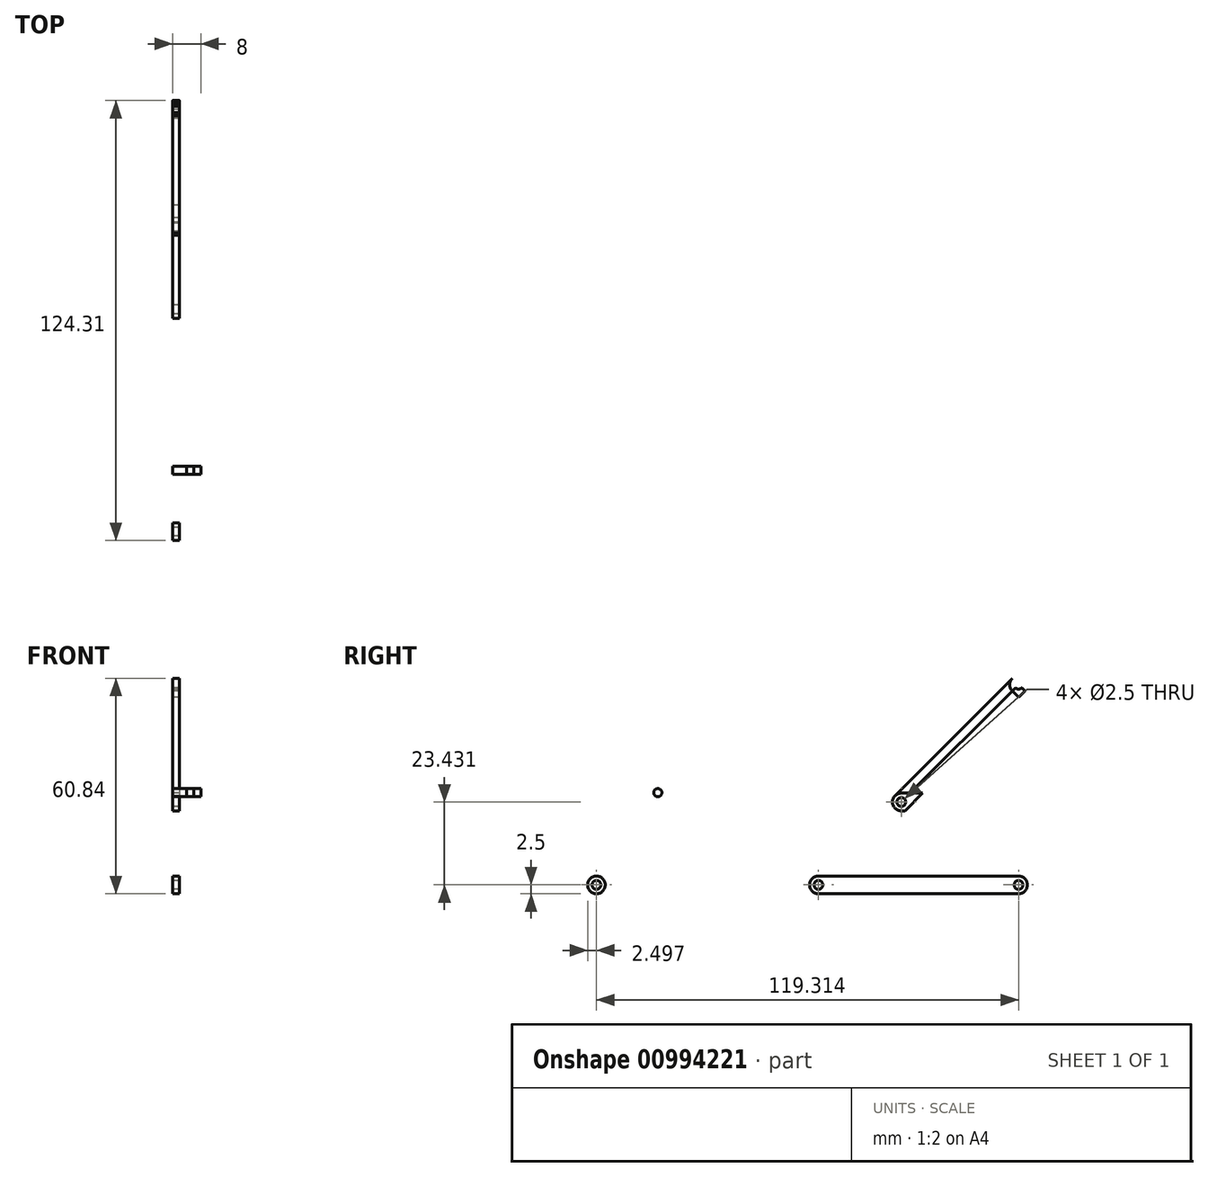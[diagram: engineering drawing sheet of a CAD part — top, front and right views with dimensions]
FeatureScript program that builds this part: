
annotation { "Feature Type Name" : "Feature", "Feature Type Description" : "" }
export const myFeature = defineFeature(function(context is Context, id is Id, definition is map)
    precondition{}
    {
        {
            assignVariable(context, id + "F0", {"name" : "thick", "anyValue" : 2});
        }
        {
            assignVariable(context, id + "F1", {"name" : "w", "anyValue" : 5});
        }
        {
            var Q0;
            Q0=qCreatedBy(makeId("Right.planeOp"),FACE);
            var sketch = newSketch(context, id + "F2", { "sketchPlane" : qUnion([Q0])});
            skLineSegment(sketch, "E0", {"start": v(0, 0) * mm, "end": v(-56.57, 56.57) * mm});
            skArc(sketch, "E1.0.startCap", {"start": v(1.77, 1.77) * mm, "mid": v(1.77, -1.77) * mm, "end": v(-1.77, -1.77) * mm});
            skArc(sketch, "E1.0.endCap", {"start": v(-58.34, 54.8) * mm, "mid": v(-58.34, 58.34) * mm, "end": v(-54.8, 58.34) * mm});
            skLineSegment(sketch, "E1.0.left", {"start": v(-1.77, -1.77) * mm, "end": v(-58.34, 54.8) * mm});
            skLineSegment(sketch, "E1.0.right", {"start": v(1.77, 1.77) * mm, "end": v(-54.8, 58.34) * mm});
            skLineSegment(sketch, "E2", {"start": v(-56.57, 56.57) * mm, "end": v(-113.14, 0) * mm});
            skArc(sketch, "E3.0.startCap", {"start": v(-58.34, 58.34) * mm, "mid": v(-54.8, 58.34) * mm, "end": v(-54.8, 54.8) * mm});
            skArc(sketch, "E3.0.endCap", {"start": v(-111.37, -1.77) * mm, "mid": v(-114.9, -1.77) * mm, "end": v(-114.9, 1.77) * mm});
            skLineSegment(sketch, "E3.0.left", {"start": v(-54.8, 54.8) * mm, "end": v(-111.37, -1.77) * mm});
            skLineSegment(sketch, "E3.0.right", {"start": v(-58.34, 58.34) * mm, "end": v(-114.9, 1.77) * mm});
            skLineSegment(sketch, "E4", {"start": v(0, 0) * mm, "end": v(230.96, 0) * mm, "construction": true});
            skLineSegment(sketch, "E5", {"start": v(-56.57, 0) * mm, "end": v(-113.14, 0) * mm});
            skArc(sketch, "E6.0.startCap", {"start": v(-56.57, 2.5) * mm, "mid": v(-54.07, 0) * mm, "end": v(-56.57, -2.5) * mm});
            skArc(sketch, "E6.0.endCap", {"start": v(-113.14, -2.5) * mm, "mid": v(-115.64, 0) * mm, "end": v(-113.14, 2.5) * mm});
            skLineSegment(sketch, "E6.0.left", {"start": v(-56.57, -2.5) * mm, "end": v(-113.14, -2.5) * mm});
            skLineSegment(sketch, "E6.0.right", {"start": v(-56.57, 2.5) * mm, "end": v(-113.14, 2.5) * mm});
            skLineSegment(sketch, "E7", {"start": v(-56.57, 56.57) * mm, "end": v(-56.57, -230.62) * mm, "construction": true});
            skLineSegment(sketch, "E8", {"start": v(0, 0) * mm, "end": v(0, 80) * mm, "construction": true});
            skArc(sketch, "E9", {"start": v(0, 0) * mm, "mid": v(-36.42, 8.77) * mm, "end": v(-64.86, 33.16) * mm, "construction": true});
            skLineSegment(sketch, "E10", {"start": v(-56.57, 23.43) * mm, "end": v(-89.7, 23.43) * mm});
            skArc(sketch, "E11.0.startCap", {"start": v(-56.57, 25.93) * mm, "mid": v(-54.07, 23.43) * mm, "end": v(-56.57, 20.93) * mm});
            skArc(sketch, "E11.0.endCap", {"start": v(-89.7, 20.93) * mm, "mid": v(-92.2, 23.43) * mm, "end": v(-89.7, 25.93) * mm});
            skLineSegment(sketch, "E11.0.left", {"start": v(-56.57, 20.93) * mm, "end": v(-89.7, 20.93) * mm});
            skLineSegment(sketch, "E11.0.right", {"start": v(-56.57, 25.93) * mm, "end": v(-89.7, 25.93) * mm});
            skLineSegment(sketch, "E12", {"start": v(-56.57, 23.43) * mm, "end": v(-23.43, 23.43) * mm, "construction": true});
            skCircle(sketch, "E13", {"center": v(-175.88, 0) * mm, "radius": 2.5 * mm});
            skCircle(sketch, "E14", {"center": v(-158.53, 26.07) * mm, "radius": 1.15 * mm});
            skSolve(sketch);
        }
        {
            var Q0;
            Q0=makeQuery(id+"F2.imprint","IMPRINT",FACE,{"disambiguationData":[TD([[makeQuery(id+"F2.imprint","IMPRINT",EDGE,{"derivedFrom":sQuery(id+"F2.wireOp",EDGE,"E1.0.startCap")}),-1.0]])]});
            var Q1;
            {var subQ0=sQuery(id+"F2.wireOp",EDGE,"E2");var subQ1=sQuery(id+"F2.wireOp",EDGE,"E0");var subQ2=makeQuery(id+"F2.imprint","INTERSECT",VERTEX,{"derivedFrom":[subQ1,subQ0]});Q1=makeQuery(id+"F2.imprint","IMPRINT",FACE,{"disambiguationData":[TD([[makeQuery(id+"F2.imprint","IMPRINT",EDGE,{"disambiguationData":[TD([[subQ2,1.0]])],"derivedFrom":subQ1}),1.0]])]});}
            var Q2;
            {var subQ3=sQuery(id+"F2.wireOp",EDGE,"E1.0.endCap");Q2=makeQuery(id+"F2.imprint","IMPRINT",FACE,{"disambiguationData":[TD([[makeQuery(id+"F2.imprint","IMPRINT",EDGE,{"derivedFrom":subQ3}),-1.0]])]});}
            extrude(context, id + "F3", {"entities" : qUnion([Q0, Q1, Q2]), "depth" : (getVariable(context, 'thick')) * mm, "offsetDistance" : 25 * mm});
        }
        {
            var Q0;
            {var subQ2=sQuery(id+"F2.wireOp",EDGE,"E3.0.endCap");Q0=makeQuery(id+"F2.imprint","IMPRINT",FACE,{"disambiguationData":[TD([[makeQuery(id+"F2.imprint","IMPRINT",EDGE,{"derivedFrom":subQ2}),1.0]])]});}
            var Q1;
            {var subQ0=sQuery(id+"F2.wireOp",EDGE,"E5");var subQ1=sQuery(id+"F2.wireOp",EDGE,"E2");var subQ2=makeQuery(id+"F2.imprint","INTERSECT",VERTEX,{"derivedFrom":[subQ1,subQ0]});Q1=makeQuery(id+"F2.imprint","IMPRINT",FACE,{"disambiguationData":[TD([[makeQuery(id+"F2.imprint","IMPRINT",EDGE,{"disambiguationData":[TD([[subQ2,1.0]])],"derivedFrom":subQ1}),1.0]])]});}
            var Q2;
            {var subQ5=sQuery(id+"F2.wireOp",EDGE,"E3.0.endCap");Q2=makeQuery(id+"F2.imprint","IMPRINT",FACE,{"disambiguationData":[TD([[makeQuery(id+"F2.imprint","IMPRINT",EDGE,{"derivedFrom":subQ5}),-1.0]])]});}
            extrude(context, id + "F4", {"entities" : qUnion([Q0, Q1, Q2]), "depth" : (getVariable(context, 'thick')) * mm, "offsetDistance" : 25 * mm});
        }
        {
            var Q0;
            Q0=sQuery(id+"F2.wireOp",VERTEX,"E5.start");
            var Q1;
            Q1=sQuery(id+"F2.wireOp",VERTEX,"E2.end");
            var Q2;
            Q2=sQuery(id+"F2.wireOp",VERTEX,"E0.start");
            var Q3;
            Q3=sQuery(id+"F2.wireOp",VERTEX,"E0.end");
            var Q4;
            Q4=makeQuery(id+"F3.opExtrude","SWEPT_BODY",BODY,{"disambiguationData":[OSD([sQuery(id+"F2.wireOp",EDGE,"E1.0.startCap"),sQuery(id+"F2.wireOp",EDGE,"E1.0.endCap"),sQuery(id+"F2.wireOp",EDGE,"E1.0.left"),sQuery(id+"F2.wireOp",EDGE,"E1.0.right"),sQuery(id+"F2.wireOp",EDGE,"E3.0.startCap")])]});
            var Q5;
            Q5=makeQuery(id+"F4.opExtrude","SWEPT_BODY",BODY,{"disambiguationData":[OSD([sQuery(id+"F2.wireOp",EDGE,"E6.0.startCap"),sQuery(id+"F2.wireOp",EDGE,"E6.0.endCap"),sQuery(id+"F2.wireOp",EDGE,"E6.0.left"),sQuery(id+"F2.wireOp",EDGE,"E6.0.right")])]});
            hole(context, id + "F5", {"style" : HoleStyle.SIMPLE, "endStyle" : HoleEndStyle.THROUGH, "oppositeDirection" : true, "holeDiameter" : (getVariable(context, 'w') / 2) * mm, "majorDiameter" : 5 * mm, "isTappedThrough" : true, "tappedDepth" : 12 * mm, "tapClearance" : 3, "locations" : qUnion([Q0, Q1, Q2, Q3]), "scope" : qUnion([Q4, Q5])});
        }
        {
            var Q0;
            {var subQ0=sQuery(id+"F2.wireOp",EDGE,"E11.0.startCap");Q0=makeQuery(id+"F2.imprint","IMPRINT",FACE,{"disambiguationData":[TD([[makeQuery(id+"F2.imprint","IMPRINT",EDGE,{"derivedFrom":subQ0}),-1.0]])]});}
            var Q1;
            {var subQ0=sQuery(id+"F2.wireOp",EDGE,"E10");var subQ1=sQuery(id+"F2.wireOp",EDGE,"E2");var subQ2=makeQuery(id+"F2.imprint","INTERSECT",VERTEX,{"derivedFrom":[subQ1,subQ0]});Q1=makeQuery(id+"F2.imprint","IMPRINT",FACE,{"disambiguationData":[TD([[makeQuery(id+"F2.imprint","IMPRINT",EDGE,{"disambiguationData":[TD([[subQ2,1.0]])],"derivedFrom":subQ1}),1.0]])]});}
            var Q2;
            {var subQ4=sQuery(id+"F2.wireOp",EDGE,"E2");var subQ6=makeQuery(id+"F2.imprint","INTERSECT",VERTEX,{"derivedFrom":[subQ4,sQuery(id+"F2.wireOp",EDGE,"E10")]});Q2=makeQuery(id+"F2.imprint","IMPRINT",FACE,{"disambiguationData":[TD([[makeQuery(id+"F2.imprint","IMPRINT",EDGE,{"disambiguationData":[TD([[subQ6,1.0]])],"derivedFrom":subQ4}),-1.0]])]});}
            var Q3;
            {var subQ0=sQuery(id+"F2.wireOp",EDGE,"E10");var subQ1=sQuery(id+"F2.wireOp",EDGE,"E2");var subQ2=makeQuery(id+"F2.imprint","INTERSECT",VERTEX,{"derivedFrom":[subQ1,subQ0]});Q3=makeQuery(id+"F2.imprint","IMPRINT",FACE,{"disambiguationData":[TD([[makeQuery(id+"F2.imprint","IMPRINT",EDGE,{"disambiguationData":[TD([[subQ2,-1.0]])],"derivedFrom":subQ1}),1.0]])]});}
            extrude(context, id + "F6", {"entities" : qUnion([Q0, Q1, Q2, Q3]), "depth" : (getVariable(context, 'thick')) * mm, "offsetDistance" : 25 * mm});
        }
        {
            var Q0;
            Q0=sQuery(id+"F2.wireOp",VERTEX,"E10.end");
            var Q1;
            Q1=sQuery(id+"F2.wireOp",VERTEX,"E10.start");
            var Q2;
            Q2=makeQuery(id+"F6.opExtrude","SWEPT_BODY",BODY,{"disambiguationData":[OSD([sQuery(id+"F2.wireOp",EDGE,"E11.0.startCap"),sQuery(id+"F2.wireOp",EDGE,"E11.0.endCap"),sQuery(id+"F2.wireOp",EDGE,"E11.0.left"),sQuery(id+"F2.wireOp",EDGE,"E11.0.right")])]});
            hole(context, id + "F7", {"style" : HoleStyle.SIMPLE, "endStyle" : HoleEndStyle.THROUGH, "oppositeDirection" : true, "holeDiameter" : (getVariable(context, 'w') / 2) * mm, "majorDiameter" : 5 * mm, "isTappedThrough" : true, "tappedDepth" : 12 * mm, "tapClearance" : 3, "locations" : qUnion([Q0, Q1]), "scope" : qUnion([Q2])});
        }
        {
            var Q0;
            Q0=sQuery(id+"F2.wireOp",VERTEX,"E12.end");
            var Q1;
            Q1=makeQuery(id+"F3.opExtrude","SWEPT_BODY",BODY,{"disambiguationData":[OSD([sQuery(id+"F2.wireOp",EDGE,"E1.0.startCap"),sQuery(id+"F2.wireOp",EDGE,"E1.0.endCap"),sQuery(id+"F2.wireOp",EDGE,"E1.0.left"),sQuery(id+"F2.wireOp",EDGE,"E1.0.right"),sQuery(id+"F2.wireOp",EDGE,"E3.0.startCap")])]});
            hole(context, id + "F8", {"style" : HoleStyle.SIMPLE, "endStyle" : HoleEndStyle.THROUGH, "oppositeDirection" : true, "holeDiameter" : (getVariable(context, 'w') / 2) * mm, "majorDiameter" : 5 * mm, "isTappedThrough" : true, "tappedDepth" : 12 * mm, "tapClearance" : 3, "locations" : qUnion([Q0]), "scope" : qUnion([Q1])});
        }
        {
            var Q0;
            Q0=makeQuery(id+"F2.imprint","IMPRINT",FACE,{"disambiguationData":[TD([[makeQuery(id+"F2.imprint","IMPRINT",EDGE,{"derivedFrom":sQuery(id+"F2.wireOp",EDGE,"E13")}),1.0]])]});
            extrude(context, id + "F9", {"entities" : qUnion([Q0]), "depth" : (getVariable(context, 'thick')) * mm, "offsetDistance" : 25 * mm});
        }
        {
            var Q0;
            Q0=sQuery(id+"F2.wireOp",VERTEX,"E13.center");
            var Q1;
            Q1=makeQuery(id+"F9.opExtrude","SWEPT_BODY",BODY,{"disambiguationData":[OSD([sQuery(id+"F2.wireOp",EDGE,"E13")])]});
            hole(context, id + "F10", {"style" : HoleStyle.SIMPLE, "endStyle" : HoleEndStyle.THROUGH, "oppositeDirection" : true, "holeDiameter" : (getVariable(context, 'w') / 2) * mm, "majorDiameter" : 5 * mm, "isTappedThrough" : true, "tappedDepth" : 12 * mm, "tapClearance" : 3, "locations" : qUnion([Q0]), "scope" : qUnion([Q1])});
        }
        {
            var Q0;
            Q0=makeQuery(id+"F2.imprint","IMPRINT",FACE,{"disambiguationData":[TD([[makeQuery(id+"F2.imprint","IMPRINT",EDGE,{"derivedFrom":sQuery(id+"F2.wireOp",EDGE,"E14")}),1.0]])]});
            extrude(context, id + "F11", {"entities" : qUnion([Q0]), "depth" : (getVariable(context, 'thick') * 2) * mm, "offsetDistance" : 25 * mm});
        }
        {
            var Q0;
            Q0=makeQuery(id+"F2.imprint","IMPRINT",FACE,{"disambiguationData":[TD([[makeQuery(id+"F2.imprint","IMPRINT",EDGE,{"derivedFrom":sQuery(id+"F2.wireOp",EDGE,"E14")}),1.0]])]});
            extrude(context, id + "F12", {"entities" : qUnion([Q0]), "depth" : (getVariable(context, 'thick') * 3) * mm, "offsetDistance" : 25 * mm});
        }
        {
            var Q0;
            Q0=makeQuery(id+"F2.imprint","IMPRINT",FACE,{"disambiguationData":[TD([[makeQuery(id+"F2.imprint","IMPRINT",EDGE,{"derivedFrom":sQuery(id+"F2.wireOp",EDGE,"E14")}),1.0]])]});
            extrude(context, id + "F13", {"entities" : qUnion([Q0]), "depth" : (getVariable(context, 'thick') * 4) * mm, "offsetDistance" : 25 * mm});
        }
    });
